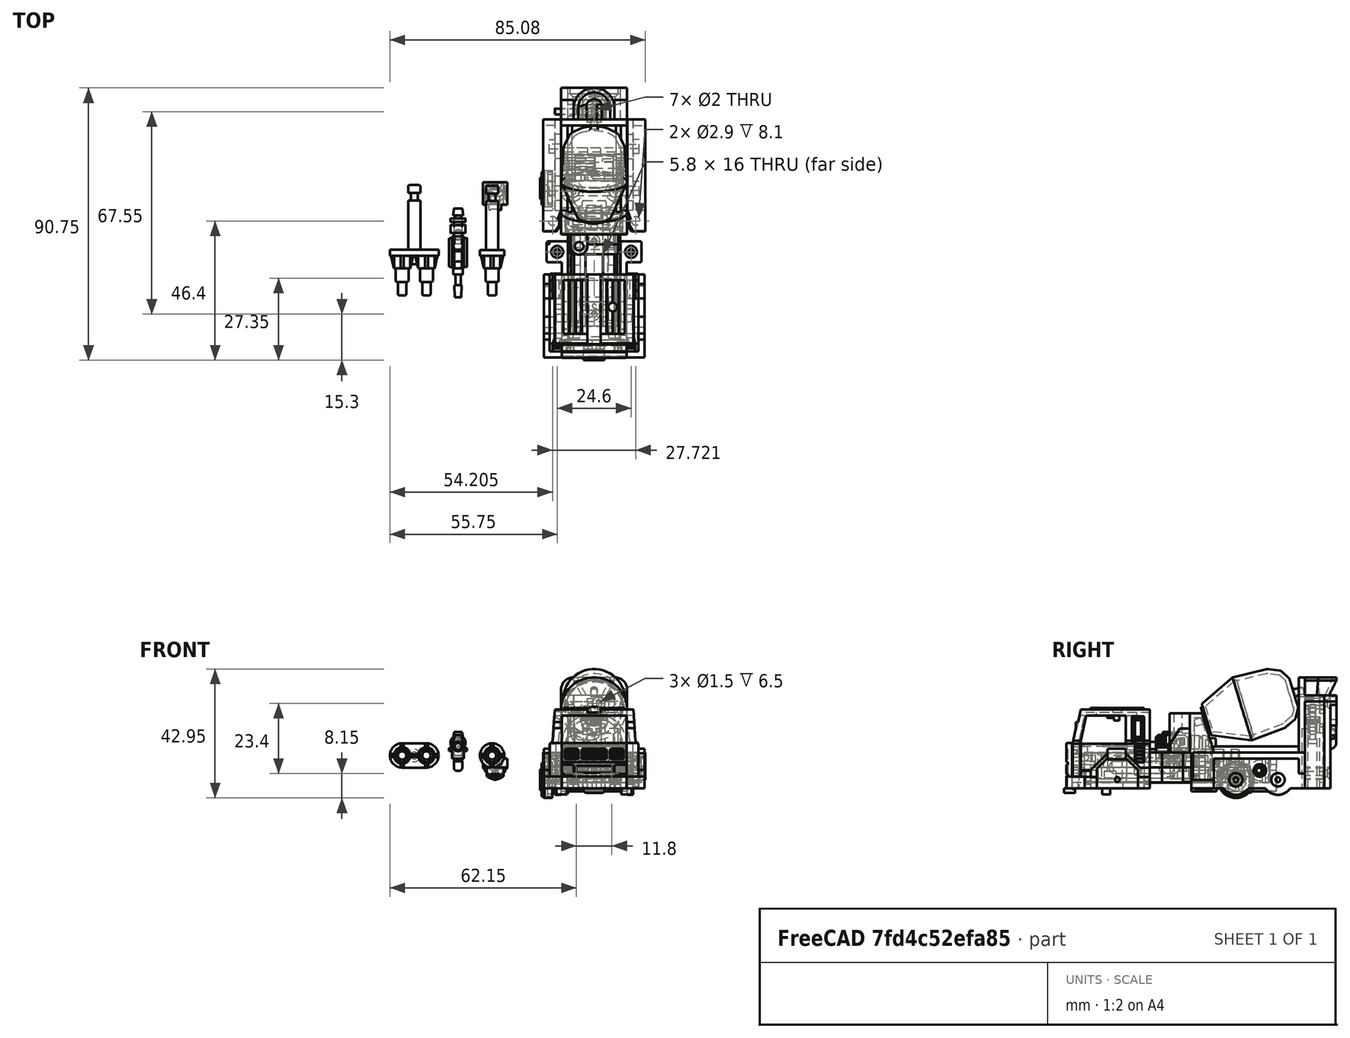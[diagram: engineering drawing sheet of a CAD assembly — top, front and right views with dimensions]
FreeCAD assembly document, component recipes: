
FREECAD ASSEMBLY — COMPONENT RECIPES ("MixMaster")

This assembly document has 25 components, labeled P0..P24 below (a component is one placed body or linked part). 24 of them carry a construction recipe — the FreeCAD feature program that regenerates the part from scratch, quoted from this document or its linked companion documents; the rest are supplied as boundary geometry only. No exploded tour is included for this assembly.
NOTE — document 4 of 4 of this assembly tour. The two overview renders and the header above are repeated from document 1; the component sections below continue where the previous document stopped.
COMPONENT P18 — recipe-attached ("Tire2", modeled in this document).
Construction recipe (the document's own serialized feature program — sketch geometry with constraints, then the solid features built on it; lengths are millimeters unless a unit is written):

FEATURE [Sketcher::SketchObject] Sketch097
  ArcFitTolerance = 1e-06
  AttachmentSupport = -> [XY_Plane008]
  FullyConstrained = true
  MakeInternals = false
  MapMode = 5
  sketch-geometry (1):
    g0: Circle CenterX=0 CenterY=0 CenterZ=0 NormalX=0 NormalY=0 NormalZ=1 AngleXU=0 Radius=6.05
  constraints (2):
    c: Coincident(g0,g-1)
    c: Diameter(g0) = 12.1
FEATURE [PartDesign::Pad] Pad067
  Direction = (0,0,1)
  Length = 3.6
  Length2 = 10
  Profile = -> Sketch097
  ReferenceAxis = -> Sketch097 [N_Axis]
  Refine = true
  Suppressed = false
  Type = 0
FEATURE [Sketcher::SketchObject] Sketch098
  ArcFitTolerance = 1e-06
  AttachmentSupport = -> [Pad067]
  FullyConstrained = true
  MakeInternals = false
  MapMode = 5
  Placement = pos=(0,0,3.6) rot=(0,0,1;0rad)
  sketch-geometry (1):
    g0: Circle CenterX=0 CenterY=0 CenterZ=0 NormalX=0 NormalY=0 NormalZ=1 AngleXU=0 Radius=3.55
  constraints (2):
    c: Coincident(g0,g-1)
    c: Diameter(g0) = 7.1
FEATURE [PartDesign::Pad] Pad068
  BaseFeature = -> Pad067
  Direction = (0,0,1)
  Length = 0.5
  Length2 = 10
  Profile = -> Sketch098
  ReferenceAxis = -> Sketch098 [N_Axis]
  Refine = true
  Suppressed = false
  Type = 0
FEATURE [Sketcher::SketchObject] Sketch099
  ArcFitTolerance = 1e-06
  AttachmentSupport = -> [Pad068]
  ExternalGeometry = -> [Pad068]
  FullyConstrained = true
  MakeInternals = false
  MapMode = 5
  Placement = pos=(0,0,3.6) rot=(0,0,1;0rad)
  sketch-geometry (2):
    g0: Circle CenterX=0 CenterY=0 CenterZ=0 NormalX=0 NormalY=0 NormalZ=1 AngleXU=0 Radius=5
    g1: Circle CenterX=0 CenterY=0 CenterZ=0 NormalX=0 NormalY=0 NormalZ=1 AngleXU=0 Radius=6.05
  constraints (5):
    c: Diameter(g0) = 10
    c: Coincident(g1,g0)
    c: Diameter(g-3) = 12.1
    c: Diameter(g1) = 12.1
    c: Coincident(g0,g-1)
FEATURE [PartDesign::Pocket] Pocket091
  BaseFeature = -> Pad068
  Direction = (0,0,-1)
  Length = 1
  Length2 = 5
  Profile = -> Sketch099
  ReferenceAxis = -> Sketch099 [N_Axis]
  Refine = true
  Suppressed = false
  Type = 0
FEATURE [Sketcher::SketchObject] Sketch100
  ArcFitTolerance = 1e-06
  AttachmentSupport = -> [Pocket091]
  ExternalGeometry = -> [Pocket091]
  FullyConstrained = true
  MakeInternals = false
  MapMode = 5
  Placement = pos=(0,0,3.6) rot=(0,0,1;0rad)
  sketch-geometry (50):
    g0: Circle [constr] CenterX=0 CenterY=0 CenterZ=0 NormalX=0 NormalY=0 NormalZ=1 AngleXU=0 Radius=6.05
    g1: LineSegment StartX=4e-16 StartY=6.05 StartZ=0 EndX=-0.789683 EndY=5.99824 EndZ=0
    g2: LineSegment StartX=-0.789683 StartY=5.99824 StartZ=0 EndX=-1.56586 EndY=5.84385 EndZ=0
    g3: LineSegment StartX=-1.56586 StartY=5.84385 StartZ=0 EndX=-2.31523 EndY=5.58947 EndZ=0
    g4: LineSegment StartX=-2.31523 StartY=5.58947 StartZ=0 EndX=-3.025 EndY=5.23945 EndZ=0
    g5: LineSegment StartX=-3.025 StartY=5.23945 StartZ=0 EndX=-3.68301 EndY=4.79979 EndZ=0
    g6: LineSegment StartX=-3.68301 StartY=4.79979 StartZ=0 EndX=-4.278 EndY=4.278 EndZ=0
    g7: LineSegment StartX=-4.278 StartY=4.278 StartZ=0 EndX=-4.79979 EndY=3.68301 EndZ=0
    g8: LineSegment StartX=-4.79979 StartY=3.68301 StartZ=0 EndX=-5.23945 EndY=3.025 EndZ=0
    g9: LineSegment StartX=-5.23945 StartY=3.025 StartZ=0 EndX=-5.58947 EndY=2.31523 EndZ=0
    g10: LineSegment StartX=-5.58947 StartY=2.31523 StartZ=0 EndX=-5.84385 EndY=1.56586 EndZ=0
    g11: LineSegment StartX=-5.84385 StartY=1.56586 StartZ=0 EndX=-5.99824 EndY=0.789683 EndZ=0
    g12: LineSegment StartX=-5.99824 StartY=0.789683 StartZ=0 EndX=-6.05 EndY=4e-16 EndZ=0
    g13: LineSegment StartX=-6.05 StartY=4e-16 StartZ=0 EndX=-5.99824 EndY=-0.789683 EndZ=0
    g14: LineSegment StartX=-5.99824 StartY=-0.789683 StartZ=0 EndX=-5.84385 EndY=-1.56586 EndZ=0
    g15: LineSegment StartX=-5.84385 StartY=-1.56586 StartZ=0 EndX=-5.58947 EndY=-2.31523 EndZ=0
    g16: LineSegment StartX=-5.58947 StartY=-2.31523 StartZ=0 EndX=-5.23945 EndY=-3.025 EndZ=0
    g17: LineSegment StartX=-5.23945 StartY=-3.025 StartZ=0 EndX=-4.79979 EndY=-3.68301 EndZ=0
    g18: LineSegment StartX=-4.79979 StartY=-3.68301 StartZ=0 EndX=-4.278 EndY=-4.278 EndZ=0
    g19: LineSegment StartX=-4.278 StartY=-4.278 StartZ=0 EndX=-3.68301 EndY=-4.79979 EndZ=0
    g20: LineSegment StartX=-3.68301 StartY=-4.79979 StartZ=0 EndX=-3.025 EndY=-5.23945 EndZ=0
    g21: LineSegment StartX=-3.025 StartY=-5.23945 StartZ=0 EndX=-2.31523 EndY=-5.58947 EndZ=0
    g22: LineSegment StartX=-2.31523 StartY=-5.58947 StartZ=0 EndX=-1.56586 EndY=-5.84385 EndZ=0
    g23: LineSegment StartX=-1.56586 StartY=-5.84385 StartZ=0 EndX=-0.789683 EndY=-5.99824 EndZ=0
    g24: LineSegment StartX=-0.789683 StartY=-5.99824 StartZ=0 EndX=-1e-16 EndY=-6.05 EndZ=0
    g25: LineSegment StartX=-1e-16 StartY=-6.05 StartZ=0 EndX=0.789683 EndY=-5.99824 EndZ=0
    g26: LineSegment StartX=0.789683 StartY=-5.99824 StartZ=0 EndX=1.56586 EndY=-5.84385 EndZ=0
    g27: LineSegment StartX=1.56586 StartY=-5.84385 StartZ=0 EndX=2.31523 EndY=-5.58947 EndZ=0
    g28: LineSegment StartX=2.31523 StartY=-5.58947 StartZ=0 EndX=3.025 EndY=-5.23945 EndZ=0
    g29: LineSegment StartX=3.025 StartY=-5.23945 StartZ=0 EndX=3.68301 EndY=-4.79979 EndZ=0
    g30: LineSegment StartX=3.68301 StartY=-4.79979 StartZ=0 EndX=4.278 EndY=-4.278 EndZ=0
    g31: LineSegment StartX=4.278 StartY=-4.278 StartZ=0 EndX=4.79979 EndY=-3.68301 EndZ=0
    g32: LineSegment StartX=4.79979 StartY=-3.68301 StartZ=0 EndX=5.23945 EndY=-3.025 EndZ=0
    g33: LineSegment StartX=5.23945 StartY=-3.025 StartZ=0 EndX=5.58947 EndY=-2.31523 EndZ=0
    g34: LineSegment StartX=5.58947 StartY=-2.31523 StartZ=0 EndX=5.84385 EndY=-1.56586 EndZ=0
    g35: LineSegment StartX=5.84385 StartY=-1.56586 StartZ=0 EndX=5.99824 EndY=-0.789683 EndZ=0
    g36: LineSegment StartX=5.99824 StartY=-0.789683 StartZ=0 EndX=6.05 EndY=0 EndZ=0
    g37: LineSegment StartX=6.05 StartY=0 StartZ=0 EndX=5.99824 EndY=0.789683 EndZ=0
    g38: LineSegment StartX=5.99824 StartY=0.789683 StartZ=0 EndX=5.84385 EndY=1.56586 EndZ=0
    g39: LineSegment StartX=5.84385 StartY=1.56586 StartZ=0 EndX=5.58947 EndY=2.31523 EndZ=0
    g40: LineSegment StartX=5.58947 StartY=2.31523 StartZ=0 EndX=5.23945 EndY=3.025 EndZ=0
    g41: LineSegment StartX=5.23945 StartY=3.025 StartZ=0 EndX=4.79979 EndY=3.68301 EndZ=0
    g42: LineSegment StartX=4.79979 StartY=3.68301 StartZ=0 EndX=4.278 EndY=4.278 EndZ=0
    g43: LineSegment StartX=4.278 StartY=4.278 StartZ=0 EndX=3.68301 EndY=4.79979 EndZ=0
    g44: LineSegment StartX=3.68301 StartY=4.79979 StartZ=0 EndX=3.025 EndY=5.23945 EndZ=0
    g45: LineSegment StartX=3.025 StartY=5.23945 StartZ=0 EndX=2.31523 EndY=5.58947 EndZ=0
    g46: LineSegment StartX=2.31523 StartY=5.58947 StartZ=0 EndX=1.56586 EndY=5.84385 EndZ=0
    g47: LineSegment StartX=1.56586 StartY=5.84385 StartZ=0 EndX=0.789683 EndY=5.99824 EndZ=0
    g48: LineSegment StartX=0.789683 StartY=5.99824 StartZ=0 EndX=4e-16 EndY=6.05 EndZ=0
    g49: Circle [constr] CenterX=0 CenterY=0 CenterZ=0 NormalX=0 NormalY=0 NormalZ=1 AngleXU=0 Radius=6.05
  constraints (102):
    c: Coincident(g0,g-1)
    c: Coincident(g1,g2)
    c: Coincident(g2,g3)
    c: Coincident(g3,g4)
    c: Coincident(g4,g5)
    c: Coincident(g5,g6)
    c: Coincident(g6,g7)
    c: Coincident(g7,g8)
    c: Coincident(g8,g9)
    c: Coincident(g9,g10)
    c: Coincident(g10,g11)
    c: Coincident(g11,g12)
    c: Coincident(g12,g13)
    c: Coincident(g13,g14)
    c: Coincident(g14,g15)
    c: Coincident(g15,g16)
    c: Coincident(g16,g17)
    c: Coincident(g17,g18)
    c: Coincident(g18,g19)
    c: Coincident(g19,g20)
    c: Coincident(g20,g21)
    c: Coincident(g21,g22)
    c: Coincident(g22,g23)
    c: Coincident(g23,g24)
    c: Coincident(g24,g25)
    c: Coincident(g25,g26)
    c: Coincident(g26,g27)
    c: Coincident(g27,g28)
    c: Coincident(g28,g29)
    c: Coincident(g29,g30)
    c: Coincident(g30,g31)
    c: Coincident(g31,g32)
    c: Coincident(g32,g33)
    c: Coincident(g33,g34)
    c: Coincident(g34,g35)
    c: Coincident(g35,g36)
    c: Coincident(g36,g37)
    c: Coincident(g37,g38)
    c: Coincident(g38,g39)
    c: Coincident(g39,g40)
    c: Coincident(g40,g41)
    c: Coincident(g41,g42)
    c: Coincident(g42,g43)
    c: Coincident(g43,g44)
    c: Coincident(g44,g45)
    c: Coincident(g45,g46)
    c: Coincident(g46,g47)
    c: Coincident(g47,g48)
    c: Coincident(g48,g1)
    c: Equal(g1, g2-g48) x47
    c: PointOnObject(g1,g49)
    c: PointOnObject(g2,g49)
    c: PointOnObject(g3,g49)
    c: PointOnObject(g4,g49)
    c: PointOnObject(g5,g49)
    c: PointOnObject(g6,g49)
    c: PointOnObject(g7,g49)
    c: PointOnObject(g8,g49)
    c: PointOnObject(g9,g49)
    c: PointOnObject(g10,g49)
    c: PointOnObject(g11,g49)
    c: PointOnObject(g12,g49)
    c: PointOnObject(g13,g49)
    c: PointOnObject(g14,g49)
    c: PointOnObject(g15,g49)
    c: PointOnObject(g16,g49)
    c: PointOnObject(g17,g49)
    c: PointOnObject(g18,g49)
    c: PointOnObject(g19,g49)
    c: PointOnObject(g20,g49)
    c: PointOnObject(g21,g49)
    c: PointOnObject(g22,g49)
    c: PointOnObject(g23,g49)
    c: PointOnObject(g24,g49)
    c: PointOnObject(g25,g49)
    c: PointOnObject(g26,g49)
    c: PointOnObject(g27,g49)
    c: PointOnObject(g28,g49)
    c: PointOnObject(g29,g49)
    c: PointOnObject(g30,g49)
    c: PointOnObject(g31,g49)
    c: PointOnObject(g32,g49)
    c: PointOnObject(g33,g49)
    c: PointOnObject(g34,g49)
    c: PointOnObject(g35,g49)
    c: PointOnObject(g36,g49)
    c: PointOnObject(g37,g49)
    c: PointOnObject(g38,g49)
    c: PointOnObject(g39,g49)
    c: PointOnObject(g40,g49)
    c: PointOnObject(g41,g49)
    c: PointOnObject(g42,g49)
    c: PointOnObject(g43,g49)
    c: PointOnObject(g44,g49)
    c: PointOnObject(g45,g49)
    c: PointOnObject(g46,g49)
    c: PointOnObject(g47,g49)
    c: PointOnObject(g48,g49)
    c: Coincident(g49,g0)
    c: PointOnObject(g48,g0)
    c: PointOnObject(g1,g-3)
    c: DistanceY(g0,g36) = 0
FEATURE [PartDesign::Pad] Pad069
  BaseFeature = -> Pocket091
  Direction = (0,0,1)
  Length = 1
  Length2 = 10
  Profile = -> Sketch100
  ReferenceAxis = -> Sketch100 [N_Axis]
  Refine = true
  Reversed = true
  Suppressed = false
  Type = 0
FEATURE [PartDesign::Chamfer] Chamfer
  Angle = 45
  Base = -> Pad069 [Edge137,Edge139,Edge141,Edge143,Edge145,Edge147,Edge149,Edge151,Edge153,Edge135,Edge133,Edge131,Edge129,Edge127,Edge125,Edge123,Edge121,Edge119,Edge117,Edge115,Edge113,Edge111,Edge109,Edge107,Edge105,Edge103,Edge101,Edge194,Edge193,Edge191,Edge189,Edge187,Edge185,Edge183,Edge181,Edge179,Edge177,Edge175,Edge173,Edge171,+8 more]
  BaseFeature = -> Pad069
  ChamferType = 0
  FlipDirection = false
  Refine = true
  Size = 0.99
  Size2 = 1
  SupportTransform = false
  Suppressed = false
  UseAllEdges = false
FEATURE [PartDesign::Pad] Pad070
  BaseFeature = -> Chamfer
  Direction = (-0.312745,0.634185,0.707107)
  Length = 0.2
  Length2 = 10
  Profile = -> Chamfer [Face44]
  Refine = true
  Suppressed = false
  Type = 0
FEATURE [PartDesign::Pad] Pad071
  BaseFeature = -> Pad070
  Direction = (0.587938,-0.392847,0.707107)
  Length = 0.2
  Length2 = 10
  Profile = -> Pad070 [Face45]
  Refine = true
  Suppressed = false
  Type = 0
FEATURE [PartDesign::Pad] Pad072
  BaseFeature = -> Pad071
  Direction = (-0.13795,0.69352,0.707107)
  Length = 0.2
  Length2 = 10
  Profile = -> Pad071 [Face48]
  Refine = true
  Suppressed = false
  Type = 0
FEATURE [PartDesign::Pad] Pad073
  BaseFeature = -> Pad072
  Direction = (0.046247,0.705593,0.707107)
  Length = 0.2
  Length2 = 10
  Profile = -> Pad072 [Face50]
  Refine = true
  Suppressed = false
  Type = 0
FEATURE [PartDesign::Pad] Pad074
  BaseFeature = -> Pad073
  Direction = (0.227292,0.669581,0.707107)
  Length = 0.2
  Length2 = 10
  Profile = -> Pad073 [Face52]
  Refine = true
  Suppressed = false
  Type = 0
FEATURE [PartDesign::Pad] Pad075
  BaseFeature = -> Pad074
  Direction = (0.392847,0.587938,0.707107)
  Length = 0.2
  Length2 = 10
  Profile = -> Pad074 [Face56]
  Refine = true
  Suppressed = false
  Type = 0
FEATURE [PartDesign::Pad] Pad076
  BaseFeature = -> Pad075
  Direction = (0.531631,0.466228,0.707107)
  Length = 0.2
  Length2 = 10
  Profile = -> Pad075 [Face60]
  Refine = true
  Suppressed = false
  Type = 0
FEATURE [PartDesign::Pad] Pad077
  BaseFeature = -> Pad076
  Direction = (0.634185,0.312745,0.707107)
  Length = 0.2
  Length2 = 10
  Profile = -> Pad076 [Face57]
  Refine = true
  Suppressed = false
  Type = 0
FEATURE [PartDesign::Pad] Pad078
  BaseFeature = -> Pad077
  Direction = (-0.466228,0.531631,0.707107)
  Length = 0.2
  Length2 = 10
  Profile = -> Pad077 [Face40]
  Refine = true
  Suppressed = false
  Type = 0
FEATURE [PartDesign::Pad] Pad079
  BaseFeature = -> Pad078
  Direction = (-0.587938,0.392847,0.707107)
  Length = 0.2
  Length2 = 10
  Profile = -> Pad078 [Face36]
  Refine = true
  Suppressed = false
  Type = 0
FEATURE [PartDesign::Pad] Pad080
  BaseFeature = -> Pad079
  Direction = (-0.669581,0.227292,0.707107)
  Length = 0.2
  Length2 = 10
  Profile = -> Pad079 [Face32]
  Refine = true
  Suppressed = false
  Type = 0
FEATURE [PartDesign::Pad] Pad081
  BaseFeature = -> Pad080
  Direction = (-0.705593,0.046247,0.707107)
  Length = 0.2
  Length2 = 10
  Profile = -> Pad080 [Face28]
  Refine = true
  Suppressed = false
  Type = 0
FEATURE [PartDesign::Pad] Pad082
  BaseFeature = -> Pad081
  Direction = (-0.69352,-0.13795,0.707107)
  Length = 0.2
  Length2 = 10
  Profile = -> Pad081 [Face24]
  Refine = true
  Suppressed = false
  Type = 0
FEATURE [PartDesign::Pad] Pad083
  BaseFeature = -> Pad082
  Direction = (-0.634185,-0.312745,0.707107)
  Length = 0.2
  Length2 = 10
  Profile = -> Pad082 [Face20]
  Refine = true
  Suppressed = false
  Type = 0
FEATURE [PartDesign::Pad] Pad084
  BaseFeature = -> Pad083
  Direction = (0.69352,0.13795,0.707107)
  Length = 0.2
  Length2 = 10
  Profile = -> Pad083 [Face53]
  Refine = true
  Suppressed = false
  Type = 0
FEATURE [PartDesign::Pad] Pad085
  BaseFeature = -> Pad084
  Direction = (0.705593,-0.046247,0.707107)
  Length = 0.2
  Length2 = 10
  Profile = -> Pad084 [Face3]
  Refine = true
  Suppressed = false
  Type = 0
FEATURE [PartDesign::Pad] Pad086
  BaseFeature = -> Pad085
  Direction = (0.669581,-0.227292,0.707107)
  Length = 0.2
  Length2 = 10
  Profile = -> Pad085 [Face17]
  Refine = true
  Suppressed = false
  Type = 0
FEATURE [PartDesign::Pad] Pad087
  BaseFeature = -> Pad086
  Direction = (0.466228,-0.531631,0.707107)
  Length = 0.2
  Length2 = 10
  Profile = -> Pad086 [Face99]
  Refine = true
  Suppressed = false
  Type = 0
FEATURE [PartDesign::Pad] Pad088
  BaseFeature = -> Pad087
  Direction = (-0.531631,-0.466228,0.707107)
  Length = 0.2
  Length2 = 10
  Profile = -> Pad087 [Face75]
  Refine = true
  Suppressed = false
  Type = 0
FEATURE [PartDesign::Pad] Pad089
  BaseFeature = -> Pad088
  Direction = (-0.392847,-0.587938,0.707107)
  Length = 0.2
  Length2 = 10
  Profile = -> Pad088 [Face79]
  Refine = true
  Suppressed = false
  Type = 0
FEATURE [PartDesign::Pad] Pad090
  BaseFeature = -> Pad089
  Direction = (-0.227292,-0.669581,0.707107)
  Length = 0.2
  Length2 = 10
  Profile = -> Pad089 [Face83]
  Refine = true
  Suppressed = false
  Type = 0
FEATURE [PartDesign::Pad] Pad091
  BaseFeature = -> Pad090
  Direction = (-0.046247,-0.705593,0.707107)
  Length = 0.2
  Length2 = 10
  Profile = -> Pad090 [Face87]
  Refine = true
  Suppressed = false
  Type = 0
FEATURE [PartDesign::Pad] Pad092
  BaseFeature = -> Pad091
  Direction = (0.312745,-0.634185,0.707107)
  Length = 0.2
  Length2 = 10
  Profile = -> Pad091 [Face95]
  Refine = true
  Suppressed = false
  Type = 0
FEATURE [PartDesign::Pad] Pad093
  BaseFeature = -> Pad092
  Direction = (0.13795,-0.69352,0.707107)
  Length = 0.2
  Length2 = 10
  Profile = -> Pad092 [Face91]
  Refine = true
  Suppressed = false
  Type = 0
FEATURE [Sketcher::SketchObject] Sketch101
  ArcFitTolerance = 1e-06
  AttachmentSupport = -> [Pad093]
  FullyConstrained = true
  MakeInternals = false
  MapMode = 5
  Placement = pos=(0,0,3.6) rot=(0,0,1;0rad)
  sketch-geometry (2):
    g0: Circle CenterX=0 CenterY=0 CenterZ=0 NormalX=0 NormalY=0 NormalZ=1 AngleXU=0 Radius=5.5
    g1: Circle CenterX=0 CenterY=0 CenterZ=0 NormalX=0 NormalY=0 NormalZ=1 AngleXU=0 Radius=4.5
  constraints (4):
    c: Coincident(g0,g-1)
    c: Diameter(g0) = 11
    c: Coincident(g1,g0)
    c: Diameter(g1) = 9
FEATURE [PartDesign::Pocket] Pocket092
  BaseFeature = -> Pad093
  Direction = (0,0,-1)
  Length = 5
  Length2 = 5
  Profile = -> Sketch101 [Edge2,Edge1]
  ReferenceAxis = -> Sketch101 [N_Axis]
  Refine = true
  Reversed = true
  Suppressed = false
  Type = 0
FEATURE [Sketcher::SketchObject] Sketch102
  ArcFitTolerance = 1e-06
  AttachmentSupport = -> [Pocket092]
  ExternalGeometry = -> [Pocket092]
  FullyConstrained = false
  MakeInternals = false
  MapMode = 5
  Placement = pos=(0,0,0) rot=(1,0,0;3.14159rad)
  sketch-geometry (2):
    g0: Circle CenterX=0 CenterY=0 CenterZ=0 NormalX=0 NormalY=0 NormalZ=1 AngleXU=0 Radius=6.05
    g1: Circle CenterX=0 CenterY=0 CenterZ=0 NormalX=0 NormalY=0 NormalZ=1 AngleXU=0 Radius=6.5
  constraints (3):
    c: Coincident(g0,g-1)
    c: Coincident(g1,g0)
    c: Diameter(g1) = 13
FEATURE [PartDesign::Pocket] Pocket093
  BaseFeature = -> Pocket092
  Direction = (0,0,1)
  Length = 5
  Length2 = 5
  Profile = -> Sketch102
  ReferenceAxis = -> Sketch102 [N_Axis]
  Refine = true
  Suppressed = false
  Type = 0
FEATURE [Sketcher::SketchObject] Sketch103
  ArcFitTolerance = 1e-06
  AttachmentSupport = -> [Pocket093]
  FullyConstrained = true
  MakeInternals = false
  MapMode = 5
  Placement = pos=(0,0,4.1) rot=(0,0,1;0rad)
  sketch-geometry (1):
    g0: Circle CenterX=0 CenterY=0 CenterZ=0 NormalX=0 NormalY=0 NormalZ=1 AngleXU=0 Radius=1.05
  constraints (2):
    c: Coincident(g0,g-1)
    c: Diameter(g0) = 2.1
FEATURE [PartDesign::Pocket] Pocket094
  BaseFeature = -> Pocket093
  Direction = (0,0,-1)
  Length = 5
  Length2 = 5
  Profile = -> Sketch103
  ReferenceAxis = -> Sketch103 [N_Axis]
  Refine = true
  Suppressed = false
  Type = 0
FEATURE [Sketcher::SketchObject] Sketch104
  ArcFitTolerance = 1e-06
  AttachmentSupport = -> [Pocket094]
  FullyConstrained = true
  MakeInternals = false
  MapMode = 5
  Placement = pos=(0,0,4.1) rot=(0,0,1;0rad)
  sketch-geometry (1):
    g0: Circle CenterX=0 CenterY=0 CenterZ=0 NormalX=0 NormalY=0 NormalZ=1 AngleXU=0 Radius=1.75
  constraints (2):
    c: Coincident(g0,g-1)
    c: Diameter(g0) = 3.5
FEATURE [PartDesign::Pocket] Pocket095
  BaseFeature = -> Pocket094
  Direction = (0,0,-1)
  Length = 1
  Length2 = 5
  Profile = -> Sketch104
  ReferenceAxis = -> Sketch104 [N_Axis]
  Refine = true
  Suppressed = false
  Type = 0
FEATURE [Sketcher::SketchObject] Sketch105
  ArcFitTolerance = 1e-06
  AttachmentSupport = -> [Pocket095]
  ExternalGeometry = -> [Pocket095]
  FullyConstrained = true
  MakeInternals = false
  MapMode = 5
  Placement = pos=(0,0,4.1) rot=(0,0,1;0rad)
  sketch-geometry (12):
    g0: Circle CenterX=0 CenterY=2.65 CenterZ=0 NormalX=0 NormalY=0 NormalZ=1 AngleXU=0 Radius=0.25
    g1: Circle CenterX=2.65 CenterY=0 CenterZ=0 NormalX=0 NormalY=0 NormalZ=1 AngleXU=0 Radius=0.25
    g2: Circle CenterX=0 CenterY=-2.65 CenterZ=0 NormalX=0 NormalY=0 NormalZ=1 AngleXU=0 Radius=0.25
    g3: Circle CenterX=-2.65 CenterY=0 CenterZ=0 NormalX=0 NormalY=0 NormalZ=1 AngleXU=0 Radius=0.25
    g4: Circle CenterX=1.87383 CenterY=1.87383 CenterZ=0 NormalX=0 NormalY=0 NormalZ=1 AngleXU=0 Radius=0.25
    g5: Circle CenterX=1.87383 CenterY=-1.87383 CenterZ=0 NormalX=0 NormalY=0 NormalZ=1 AngleXU=0 Radius=0.25
    g6: Circle CenterX=-1.87383 CenterY=-1.87383 CenterZ=0 NormalX=0 NormalY=0 NormalZ=1 AngleXU=0 Radius=0.25
    g7: Circle CenterX=-1.87383 CenterY=1.87383 CenterZ=0 NormalX=0 NormalY=0 NormalZ=1 AngleXU=0 Radius=0.25
    g8: LineSegment StartX=1.87383 StartY=1.87383 StartZ=0 EndX=0 EndY=0 EndZ=0
    g9: LineSegment StartX=0 StartY=0 StartZ=0 EndX=1.87383 EndY=-1.87383 EndZ=0
    g10: LineSegment StartX=0 StartY=0 StartZ=0 EndX=-1.87383 EndY=-1.87383 EndZ=0
    g11: LineSegment StartX=0 StartY=0 StartZ=0 EndX=-1.87383 EndY=1.87383 EndZ=0
  constraints (34):
    c: PointOnObject(g0,g-2)
    c: Diameter(g-3) = 7.1
    c: Diameter(g-4) = 3.5
    c: DistanceY(g-1,g0) = 2.65
    c: Diameter(g0) = 0.5
    c: PointOnObject(g1,g-1)
    c: PointOnObject(g2,g-2)
    c: PointOnObject(g3,g-1)
    c: Diameter(g3) = 0.5
    c: Diameter(g1) = 0.5
    c: Diameter(g2) = 0.5
    c: DistanceX(g3,g-1) = 2.65
    c: DistanceX(g-1,g1) = 2.65
    c: DistanceY(g2,g-1) = 2.65
    c: Diameter(g7) = 0.5
    c: Diameter(g4) = 0.5
    c: Diameter(g5) = 0.5
    c: Diameter(g6) = 0.5
    c: Distance(g-1,g6) = 2.65
    c: Distance(g-1,g5) = 2.65
    c: Distance(g-1,g4) = 2.65
    c: Distance(g-1,g7) = 2.65
    c: Coincident(g8,g4)
    c: Coincident(g8,g-1)
    c: Angle(g-1,g8) = 0.785398
    c: Coincident(g9,g8)
    c: Coincident(g9,g5)
    c: Coincident(g10,g8)
    c: Coincident(g10,g6)
    c: Coincident(g11,g8)
    c: Coincident(g11,g7)
    c: Angle(g9,g-1) = 0.785398
    c: Angle(g-2,g10) = 2.35619
    c: Angle(g-1,g11) = 2.35619
FEATURE [PartDesign::Pocket] Pocket096
  BaseFeature = -> Pocket095
  Direction = (0,0,-1)
  Length = 0.2
  Length2 = 5
  Profile = -> Sketch105 [Edge8,Edge4,Edge7,Edge3,Edge6,Edge2,Edge5,Edge1]
  ReferenceAxis = -> Sketch105 [N_Axis]
  Refine = true
  Suppressed = false
  Type = 0
FEATURE [Sketcher::SketchObject] Sketch106
  ArcFitTolerance = 1e-06
  AttachmentSupport = -> [Pocket096]
  FullyConstrained = true
  MakeInternals = false
  MapMode = 5
  Placement = pos=(0,0,0) rot=(1,0,0;3.14159rad)
  sketch-geometry (1):
    g0: Circle CenterX=0 CenterY=0 CenterZ=0 NormalX=0 NormalY=0 NormalZ=1 AngleXU=0 Radius=2.5
  constraints (2):
    c: Coincident(g0,g-1)
    c: Diameter(g0) = 5
FEATURE [PartDesign::Pocket] Pocket097
  BaseFeature = -> Pocket096
  Direction = (0,0,1)
  Length = 1.5
  Length2 = 5
  Profile = -> Sketch106
  ReferenceAxis = -> Sketch106 [N_Axis]
  Refine = true
  Suppressed = false
  Type = 0
FEATURE [Sketcher::SketchObject] Sketch107
  ArcFitTolerance = 1e-06
  AttachmentSupport = -> [Pocket097]
  FullyConstrained = true
  MakeInternals = false
  MapMode = 5
  Placement = pos=(0,0,0) rot=(1,0,0;3.14159rad)
  sketch-geometry (2):
    g0: Circle CenterX=0 CenterY=0 CenterZ=0 NormalX=0 NormalY=0 NormalZ=1 AngleXU=0 Radius=4.75
    g1: Circle CenterX=0 CenterY=0 CenterZ=0 NormalX=0 NormalY=0 NormalZ=1 AngleXU=0 Radius=5.5
  constraints (4):
    c: Coincident(g0,g-1)
    c: Coincident(g1,g0)
    c: Diameter(g0) = 9.5
    c: Diameter(g1) = 11
FEATURE [PartDesign::Pocket] Pocket098
  BaseFeature = -> Pocket097
  Direction = (0,0,1)
  Length = 1.5
  Length2 = 5
  Profile = -> Sketch107
  ReferenceAxis = -> Sketch107 [N_Axis]
  Refine = true
  Suppressed = false
  Type = 0
FEATURE [PartDesign::Body] Body007  label="Tire1"
  AllowCompound = false
  Group = -> [Sketch097,Pad067,Sketch098,Pad068,Sketch099,Pocket091,Sketch100,Pad069,Chamfer,Pad070,Pad071,Pad072,Pad073,Pad074,Pad075,Pad076,Pad077,Pad078,Pad079,Pad080,Pad081,Pad082,Pad083,Pad084,Pad085,Pad086,Pad087,Pad088,Pad089,Pad090,Pad091,Pad092,Pad093,Sketch101,Pocket092,Sketch102,Pocket093,Sketch103,Pocket094,Sketch104,Pocket095,Sketch105,Pocket096,Sketch106,Pocket097,Sketch107,Pocket098]
  Origin = -> Origin008
  Placement = pos=(30.1,12.5,-8.1) rot=(0.707107,0,-0.707107;3.14159rad)
  Tip = -> Pocket098
COMPONENT P19 — recipe-attached ("Pre_Left_Arm", modeled in this document).
Construction recipe (the document's own serialized feature program — sketch geometry with constraints, then the solid features built on it; lengths are millimeters unless a unit is written):

FEATURE [PartDesign::SubShapeBinder] Binder002
  BindCopyOnChange = 0
  BindMode = 2
  ClaimChildren = false
  Fuse = false
  MakeFace = true
  OffsetFill = false
  OffsetIntersection = false
  OffsetJoinType = 0
  OffsetOpenResult = false
  PartialLoad = false
  Refine = true
  Relative = true
  _Version = 2
FEATURE [Sketcher::SketchObject] Sketch071
  ArcFitTolerance = 1e-06
  AttachmentSupport = -> [Binder002]
  FullyConstrained = true
  MakeInternals = false
  MapMode = 5
  Placement = pos=(5.47474,0,5.62e-14) rot=(0.57735,0.57735,0.57735;2.0944rad)
  sketch-geometry (4):
    g0: LineSegment StartX=-2 StartY=-1 StartZ=0 EndX=-2 EndY=-9 EndZ=0
    g1: LineSegment StartX=-2 StartY=-9 StartZ=0 EndX=5 EndY=-9 EndZ=0
    g2: LineSegment StartX=5 StartY=-9 StartZ=0 EndX=5 EndY=-1 EndZ=0
    g3: LineSegment StartX=5 StartY=-1 StartZ=0 EndX=-2 EndY=-1 EndZ=0
  constraints (13):
    c: Vertical(g0)
    c: Vertical(g2)
    c: Horizontal(g1)
    c: Horizontal(g3)
    c: DistanceX(g0,g-1) = 2
    c: DistanceX(g-1,g2) = 5
    c: Coincident(g2,g3)
    c: DistanceY(g3,g-1) = 1
    c: DistanceY(g0,g0) = 8
    c: Coincident(g0,g3)
    c: DistanceX(g1,g1) = 7
    c: DistanceY(g2,g2) = 8
    c: Coincident(g1,g2)
FEATURE [PartDesign::Pad] Pad058
  Direction = (1,0,1.02e-14)
  Length = 2
  Length2 = 10
  Profile = -> Sketch071
  ReferenceAxis = -> Sketch071 [N_Axis]
  Refine = true
  Suppressed = false
  Type = 0
FEATURE [Sketcher::SketchObject] Sketch072
  ArcFitTolerance = 1e-06
  AttachmentSupport = -> [Pad058]
  FullyConstrained = true
  MakeInternals = false
  MapMode = 5
  Placement = pos=(7.47474,0,7.63e-14) rot=(0.57735,0.57735,0.57735;2.0944rad)
  sketch-geometry (1):
    g0: Circle CenterX=1.5 CenterY=-5 CenterZ=0 NormalX=0 NormalY=0 NormalZ=1 AngleXU=0 Radius=3.4
  constraints (3):
    c: Diameter(g0) = 6.8
    c: DistanceY(g0,g-1) = 5
    c: DistanceX(g-1,g0) = 1.5
FEATURE [PartDesign::Pad] Pad059
  BaseFeature = -> Pad058
  Direction = (1,0,1.02e-14)
  Length = 2.7
  Length2 = 10
  Profile = -> Sketch072
  ReferenceAxis = -> Sketch072 [N_Axis]
  Refine = true
  Suppressed = false
  Type = 0
FEATURE [Sketcher::SketchObject] Sketch073
  ArcFitTolerance = 1e-06
  AttachmentSupport = -> [Pad059]
  FullyConstrained = true
  MakeInternals = false
  MapMode = 5
  Placement = pos=(10.1747,0,1.028e-13) rot=(0.57735,0.57735,0.57735;2.0944rad)
  sketch-geometry (1):
    g0: Circle CenterX=1.5 CenterY=-5 CenterZ=0 NormalX=0 NormalY=0 NormalZ=1 AngleXU=0 Radius=1.4
  constraints (3):
    c: Diameter(g0) = 2.8
    c: DistanceX(g-1,g0) = 1.5
    c: DistanceY(g0,g-1) = 5
FEATURE [PartDesign::Pocket] Pocket183
  BaseFeature = -> Pad059
  Direction = (-1,0,-1.02e-14)
  Length = 5
  Length2 = 5
  Profile = -> Sketch073
  ReferenceAxis = -> Sketch073 [N_Axis]
  Refine = true
  Suppressed = false
  Type = 0
FEATURE [PartDesign::Pad] Pad060
  BaseFeature = -> Pocket183
  Direction = (-1,0,-1.02e-14)
  Length = 2
  Length2 = 10
  Profile = -> Pocket183 [Face4]
  Refine = true
  Suppressed = false
  Type = 0
FEATURE [Sketcher::SketchObject] Sketch074
  ArcFitTolerance = 1e-06
  AttachmentSupport = -> [Pad060]
  ExternalGeometry = -> [Pad060]
  FullyConstrained = true
  MakeInternals = false
  MapMode = 5
  Placement = pos=(3.47474,0,3.55e-14) rot=(0.57735,-0.57735,-0.57735;2.0944rad)
  sketch-geometry (1):
    g0: Circle CenterX=-1.5 CenterY=-5 CenterZ=0 NormalX=0 NormalY=0 NormalZ=1 AngleXU=0 Radius=2.1
  constraints (2):
    c: Diameter(g0) = 4.2
    c: Coincident(g0,g-3)
FEATURE [PartDesign::Pocket] Pocket184
  BaseFeature = -> Pad060
  Direction = (1,0,1.02e-14)
  Length = 4.7
  Length2 = 5
  Profile = -> Sketch074
  ReferenceAxis = -> Sketch074 [N_Axis]
  Refine = true
  Suppressed = false
  Type = 0
FEATURE [Sketcher::SketchObject] Sketch075
  ArcFitTolerance = 1e-06
  AttachmentSupport = -> [Pocket184]
  ExternalGeometry = -> [Pocket184]
  FullyConstrained = true
  MakeInternals = false
  MapMode = 5
  Placement = pos=(3.47474,0,3.55e-14) rot=(0.57735,-0.57735,-0.57735;2.0944rad)
  sketch-geometry (8):
    g0: LineSegment StartX=-16.5 StartY=1 StartZ=0 EndX=-16.5 EndY=-11 EndZ=0
    g1: LineSegment StartX=-16.5 StartY=-11 StartZ=0 EndX=13.8 EndY=-11 EndZ=0
    g2: LineSegment StartX=13.8 StartY=-11 StartZ=0 EndX=13.8 EndY=1 EndZ=0
    g3: LineSegment StartX=13.8 StartY=1 StartZ=0 EndX=-16.5 EndY=1 EndZ=0
    g4: LineSegment StartX=-5 StartY=-1 StartZ=0 EndX=-5 EndY=-9 EndZ=0
    g5: LineSegment StartX=-5 StartY=-9 StartZ=0 EndX=2 EndY=-9 EndZ=0
    g6: LineSegment StartX=2 StartY=-9 StartZ=0 EndX=2 EndY=-1 EndZ=0
    g7: LineSegment StartX=2 StartY=-1 StartZ=0 EndX=-5 EndY=-1 EndZ=0
  constraints (21):
    c: Coincident(g0,g1)
    c: Coincident(g1,g2)
    c: Coincident(g2,g3)
    c: Coincident(g3,g0)
    c: Vertical(g0)
    c: Vertical(g2)
    c: Horizontal(g1)
    c: Horizontal(g3)
    c: Coincident(g4,g5)
    c: Coincident(g5,g6)
    c: Coincident(g6,g7)
    c: Coincident(g7,g4)
    c: Vertical(g6)
    c: Horizontal(g7)
    c: DistanceY(g0,g0) = 12
    c: Coincident(g4,g-5)
    c: Coincident(g4,g-5)
    c: Coincident(g5,g-4)
    c: DistanceX(g0,g4) = 11.5
    c: DistanceX(g6,g2) = 11.8
    c: DistanceY(g1,g5) = 2
FEATURE [PartDesign::Pad] Pad061
  BaseFeature = -> Pocket184
  Direction = (-1,0,-1.02e-14)
  Length = 2
  Length2 = 10
  Profile = -> Sketch075
  ReferenceAxis = -> Sketch075 [N_Axis]
  Refine = true
  Reversed = true
  Suppressed = false
  Type = 0
FEATURE [Sketcher::SketchObject] Sketch076
  ArcFitTolerance = 1e-06
  AttachmentSupport = -> [Pad061]
  ExternalGeometry = -> [Pad061]
  FullyConstrained = true
  MakeInternals = false
  MapMode = 5
  Placement = pos=(3.47474,0,3.55e-14) rot=(0.57735,-0.57735,-0.57735;2.0944rad)
  sketch-geometry (6):
    g0: LineSegment StartX=-16.5 StartY=1 StartZ=0 EndX=13.8 EndY=1 EndZ=0
    g1: LineSegment StartX=13.8 StartY=1 StartZ=0 EndX=13.8 EndY=-1 EndZ=0
    g2: LineSegment StartX=13.8 StartY=-1 StartZ=0 EndX=-14.5 EndY=-1 EndZ=0
    g3: LineSegment StartX=-14.5 StartY=-1 StartZ=0 EndX=-14.5 EndY=-6 EndZ=0
    g4: LineSegment StartX=-14.5 StartY=-6 StartZ=0 EndX=-16.5 EndY=-6 EndZ=0
    g5: LineSegment StartX=-16.5 StartY=-6 StartZ=0 EndX=-16.5 EndY=1 EndZ=0
  constraints (17):
    c: Coincident(g1,g0)
    c: Coincident(g2,g1)
    c: Horizontal(g2)
    c: Coincident(g3,g2)
    c: Vertical(g3)
    c: Coincident(g4,g3)
    c: Horizontal(g4)
    c: Coincident(g5,g4)
    c: Coincident(g5,g0)
    c: DistanceY(g2,g0) = 2
    c: DistanceY(g5,g5) = 7
    c: DistanceX(g2,g-3) = 13
    c: DistanceY(g-3,g2) = 4
    c: DistanceX(g4,g4) = 2
    c: Vertical(g1)
    c: DistanceX(g0,g-1) = 16.5
    c: Coincident(g0,g-4)
FEATURE [PartDesign::Pad] Pad062
  BaseFeature = -> Pad061
  Direction = (-1,0,-1.02e-14)
  Length = 4
  Length2 = 10
  Profile = -> Sketch076
  ReferenceAxis = -> Sketch076 [N_Axis]
  Refine = true
  Suppressed = false
  Type = 0
FEATURE [Sketcher::SketchObject] Sketch077
  ArcFitTolerance = 1e-06
  AttachmentSupport = -> [Pad062]
  ExternalGeometry = -> [Pad062]
  FullyConstrained = true
  MakeInternals = false
  MapMode = 5
  Placement = pos=(5.47474,0,5.59e-14) rot=(0.57735,0.57735,0.57735;2.0944rad)
  sketch-geometry (4):
    g0: LineSegment StartX=-13.8 StartY=1 StartZ=0 EndX=-20.8 EndY=1 EndZ=0
    g1: LineSegment StartX=-20.8 StartY=1 StartZ=0 EndX=-20.8 EndY=-11 EndZ=0
    g2: LineSegment StartX=-20.8 StartY=-11 StartZ=0 EndX=-13.8 EndY=-11 EndZ=0
    g3: LineSegment StartX=-13.8 StartY=-11 StartZ=0 EndX=-13.8 EndY=1 EndZ=0
  constraints (10):
    c: Coincident(g0,g1)
    c: Coincident(g1,g2)
    c: Coincident(g2,g3)
    c: Coincident(g3,g0)
    c: Horizontal(g0)
    c: Horizontal(g2)
    c: Vertical(g1)
    c: Coincident(g0,g-3)
    c: DistanceX(g0,g0) = 7
    c: Coincident(g2,g-3)
FEATURE [PartDesign::Pad] Pad063
  BaseFeature = -> Pad062
  Direction = (1,0,1.02e-14)
  Length = 6
  Length2 = 10
  Profile = -> Sketch077
  ReferenceAxis = -> Sketch077 [N_Axis]
  Refine = true
  Reversed = true
  Suppressed = false
  Type = 0
FEATURE [Sketcher::SketchObject] Sketch079
  ArcFitTolerance = 1e-06
  AttachmentSupport = -> [Pad063]
  ExternalGeometry = -> [Pad063]
  FullyConstrained = true
  MakeInternals = false
  MapMode = 5
  Placement = pos=(1.116e-13,0,-11) rot=(1,0,0;3.14159rad)
  sketch-geometry (4):
    g0: LineSegment StartX=5.47474 StartY=20.8 StartZ=0 EndX=-0.525259 EndY=20.8 EndZ=0
    g1: LineSegment StartX=-0.525259 StartY=20.8 StartZ=0 EndX=-0.525259 EndY=13.8 EndZ=0
    g2: LineSegment StartX=-0.525259 StartY=13.8 StartZ=0 EndX=5.47474 EndY=13.8 EndZ=0
    g3: LineSegment StartX=5.47474 StartY=13.8 StartZ=0 EndX=5.47474 EndY=20.8 EndZ=0
  constraints (10):
    c: Coincident(g0,g1)
    c: Coincident(g1,g2)
    c: Coincident(g2,g3)
    c: Coincident(g3,g0)
    c: Horizontal(g0)
    c: Horizontal(g2)
    c: Vertical(g1)
    c: Vertical(g3)
    c: Coincident(g0,g-3)
    c: Coincident(g1,g-5)
FEATURE [PartDesign::Pocket] Pocket185
  BaseFeature = -> Pad063
  Direction = (-1.01e-14,0,1)
  Length = 2.9
  Length2 = 5
  Profile = -> Sketch079
  ReferenceAxis = -> Sketch079 [N_Axis]
  Refine = true
  Suppressed = false
  Type = 0
FEATURE [Sketcher::SketchObject] Sketch080
  ArcFitTolerance = 1e-06
  AttachmentSupport = -> [Pocket185]
  ExternalGeometry = -> [Pocket185]
  FullyConstrained = true
  MakeInternals = false
  MapMode = 5
  Placement = pos=(3.47474,0,3.55e-14) rot=(0.57735,-0.57735,-0.57735;2.0944rad)
  sketch-geometry (4):
    g0: Circle CenterX=6.5 CenterY=-8.1 CenterZ=0 NormalX=0 NormalY=0 NormalZ=1 AngleXU=0 Radius=2.25
    g1: Circle CenterX=-7.5 CenterY=-8.1 CenterZ=0 NormalX=0 NormalY=0 NormalZ=1 AngleXU=0 Radius=2.25
    g2: Circle CenterX=-7.5 CenterY=-8.1 CenterZ=0 NormalX=0 NormalY=0 NormalZ=1 AngleXU=0 Radius=5
    g3: Circle CenterX=6.5 CenterY=-8.1 CenterZ=0 NormalX=0 NormalY=0 NormalZ=1 AngleXU=0 Radius=5
  constraints (10):
    c: Diameter(g0) = 4.5
    c: Diameter(g1) = 4.5
    c: DistanceY(g-4,g0) = 0
    c: DistanceY(g0,g1) = 0
    c: DistanceX(g1,g0) = 14
    c: DistanceX(g-5,g1) = 9
    c: Coincident(g2,g1)
    c: Coincident(g3,g0)
    c: Diameter(g2) = 10
    c: Diameter(g3) = 10
FEATURE [PartDesign::Pad] Pad064
  BaseFeature = -> Pocket185
  Direction = (-1,0,-1.02e-14)
  Length = 2
  Length2 = 10
  Profile = -> Sketch080
  ReferenceAxis = -> Sketch080 [N_Axis]
  Refine = true
  Reversed = true
  Suppressed = false
  Type = 0
FEATURE [Sketcher::SketchObject] Sketch081
  ArcFitTolerance = 1e-06
  AttachmentSupport = -> [Pad064]
  ExternalGeometry = -> [Pad064]
  FullyConstrained = true
  MakeInternals = false
  MapMode = 5
  Placement = pos=(3.47474,0,3.55e-14) rot=(0.57735,-0.57735,-0.57735;2.0944rad)
  sketch-geometry (1):
    g0: Circle CenterX=-1.5 CenterY=-5 CenterZ=0 NormalX=0 NormalY=0 NormalZ=1 AngleXU=0 Radius=2.1
  constraints (2):
    c: Coincident(g0,g-4)
    c: Equal(g0,g-4)
FEATURE [PartDesign::Pocket] Pocket186
  BaseFeature = -> Pad064
  Direction = (1,0,1.02e-14)
  Length = 4.7
  Length2 = 5
  Profile = -> Sketch081
  ReferenceAxis = -> Sketch081 [N_Axis]
  Refine = true
  Suppressed = false
  Type = 0
FEATURE [PartDesign::Pad] Pad065
  BaseFeature = -> Pocket186
  Direction = (-1,0,-1.02e-14)
  Length = 2
  Length2 = 10
  Profile = -> Sketch080 [Edge2,Edge1]
  ReferenceAxis = -> Sketch080 [N_Axis]
  Refine = true
  Suppressed = false
  Type = 0
FEATURE [Sketcher::SketchObject] Sketch082
  ArcFitTolerance = 1e-06
  AttachmentSupport = -> [Pad065]
  ExternalGeometry = -> [Pad065]
  FullyConstrained = true
  MakeInternals = false
  MapMode = 5
  Placement = pos=(1.47474,0,1.51e-14) rot=(0.57735,-0.57735,-0.57735;2.0944rad)
  sketch-geometry (2):
    g0: Circle CenterX=-7.5 CenterY=-8.1 CenterZ=0 NormalX=0 NormalY=0 NormalZ=1 AngleXU=0 Radius=0.75
    g1: Circle CenterX=6.5 CenterY=-8.1 CenterZ=0 NormalX=0 NormalY=0 NormalZ=1 AngleXU=0 Radius=0.75
  constraints (4):
    c: Coincident(g0,g-4)
    c: Coincident(g1,g-3)
    c: Diameter(g0) = 1.5
    c: Diameter(g1) = 1.5
FEATURE [PartDesign::Pocket] Pocket187
  BaseFeature = -> Pad065
  Direction = (1,0,1.02e-14)
  Length = 5
  Length2 = 5
  Profile = -> Sketch082
  ReferenceAxis = -> Sketch082 [N_Axis]
  Refine = true
  Suppressed = false
  Type = 0
FEATURE [Sketcher::SketchObject] Sketch083
  ArcFitTolerance = 1e-06
  AttachmentSupport = -> [Pocket187]
  ExternalGeometry = -> [Pocket187]
  FullyConstrained = true
  MakeInternals = false
  MapMode = 5
  Placement = pos=(8.16e-14,0,-8.1) rot=(1,0,0;3.14159rad)
  sketch-geometry (1):
    g0: Circle CenterX=2.62474 CenterY=17.35 CenterZ=0 NormalX=0 NormalY=0 NormalZ=1 AngleXU=0 Radius=1.45
  constraints (3):
    c: Diameter(g0) = 2.9
    c: DistanceX(g-3,g0) = 3.15
    c: DistanceY(g0,g-3) = 3.45
FEATURE [PartDesign::Pocket] Pocket188
  BaseFeature = -> Pocket187
  Direction = (-1.01e-14,0,1)
  Length = 10
  Length2 = 5
  Profile = -> Sketch083
  ReferenceAxis = -> Sketch083 [N_Axis]
  Refine = true
  Suppressed = false
  Type = 0
FEATURE [Sketcher::SketchObject] Sketch084
  ArcFitTolerance = 1e-06
  AttachmentSupport = -> [Pocket188]
  ExternalGeometry = -> [Pocket188]
  FullyConstrained = true
  MakeInternals = false
  MapMode = 5
  Placement = pos=(8.16e-14,0,-8.1) rot=(1,0,0;3.14159rad)
  sketch-geometry (3):
    g0: LineSegment StartX=5.47474 StartY=16.8 StartZ=0 EndX=4.27474 EndY=16.8 EndZ=0
    g1: LineSegment StartX=4.27474 StartY=16.8 StartZ=0 EndX=5.47474 EndY=13.8 EndZ=0
    g2: LineSegment StartX=5.47474 StartY=13.8 StartZ=0 EndX=5.47474 EndY=16.8 EndZ=0
  constraints (8):
    c: PointOnObject(g0,g-3)
    c: Horizontal(g0)
    c: Coincident(g1,g0)
    c: Coincident(g1,g-4)
    c: Coincident(g2,g1)
    c: Coincident(g2,g0)
    c: DistanceY(g2,g2) = 3
    c: DistanceX(g0,g0) = 1.2
FEATURE [PartDesign::Pocket] Pocket189
  BaseFeature = -> Pocket188
  Direction = (-1.01e-14,0,1)
  Length = 10
  Length2 = 5
  Profile = -> Sketch084
  ReferenceAxis = -> Sketch084 [N_Axis]
  Refine = true
  Suppressed = false
  Type = 0
FEATURE [Sketcher::SketchObject] Sketch085
  ArcFitTolerance = 1e-06
  AttachmentSupport = -> [Pocket189]
  ExternalGeometry = -> [Pocket189]
  FullyConstrained = true
  MakeInternals = false
  MapMode = 5
  Placement = pos=(5.47474,1.149e-13,2.532e-13) rot=(0.57735,0.57735,0.57735;2.0944rad)
  sketch-geometry (4):
    g0: LineSegment StartX=-20.8 StartY=1 StartZ=0 EndX=-20.8 EndY=-8.1 EndZ=0
    g1: LineSegment StartX=-20.8 StartY=-8.1 StartZ=0 EndX=-16.8 EndY=-8.1 EndZ=0
    g2: LineSegment StartX=-16.8 StartY=-8.1 StartZ=0 EndX=-16.8 EndY=1 EndZ=0
    g3: LineSegment StartX=-16.8 StartY=1 StartZ=0 EndX=-20.8 EndY=1 EndZ=0
  constraints (10):
    c: Coincident(g0,g1)
    c: Coincident(g1,g2)
    c: Coincident(g2,g3)
    c: Coincident(g3,g0)
    c: Vertical(g0)
    c: Vertical(g2)
    c: Horizontal(g1)
    c: Horizontal(g3)
    c: Coincident(g0,g-3)
    c: Coincident(g1,g-4)
FEATURE [PartDesign::Pocket] Pocket190
  BaseFeature = -> Pocket189
  Direction = (-1,-2.09e-14,-4.64e-14)
  Length = 0.2
  Length2 = 5
  Profile = -> Sketch085
  ReferenceAxis = -> Sketch085 [N_Axis]
  Refine = true
  Suppressed = false
  Type = 0
FEATURE [Sketcher::SketchObject] Sketch086
  ArcFitTolerance = 1e-06
  AttachmentSupport = -> [Pocket190]
  ExternalGeometry = -> [Pocket190]
  FullyConstrained = true
  MakeInternals = false
  MapMode = 5
  Placement = pos=(8.16e-14,0,-8.1) rot=(1,0,0;3.14159rad)
  sketch-geometry (3):
    g0: LineSegment StartX=5.27474 StartY=20.8 StartZ=0 EndX=3.97474 EndY=20.8 EndZ=0
    g1: LineSegment StartX=3.97474 StartY=20.8 StartZ=0 EndX=5.27474 EndY=18.8 EndZ=0
    g2: LineSegment StartX=5.27474 StartY=20.8 StartZ=0 EndX=5.27474 EndY=18.8 EndZ=0
  constraints (8):
    c: Coincident(g0,g-4)
    c: PointOnObject(g0,g-3)
    c: Coincident(g1,g0)
    c: PointOnObject(g1,g-4)
    c: Coincident(g2,g0)
    c: Coincident(g2,g1)
    c: DistanceX(g0,g0) = 1.3
    c: DistanceY(g2,g2) = 2
FEATURE [PartDesign::Pocket] Pocket191
  BaseFeature = -> Pocket190
  Direction = (-1.01e-14,0,1)
  Length = 10
  Length2 = 5
  Profile = -> Sketch086
  ReferenceAxis = -> Sketch086 [N_Axis]
  Refine = true
  Suppressed = false
  Type = 0
FEATURE [Sketcher::SketchObject] Sketch087
  ArcFitTolerance = 1e-06
  AttachmentSupport = -> [Pocket191]
  ExternalGeometry = -> [Pocket191]
  FullyConstrained = true
  MakeInternals = false
  MapMode = 5
  Placement = pos=(0,-20.8,0) rot=(1,0,0;1.5708rad)
  sketch-geometry (12):
    g0: LineSegment StartX=-0.525259 StartY=-0.2 StartZ=0 EndX=-0.525259 EndY=-0.4 EndZ=0
    g1: LineSegment StartX=-0.525259 StartY=-0.4 StartZ=0 EndX=3.97474 EndY=-0.4 EndZ=0
    g2: LineSegment StartX=3.97474 StartY=-0.4 StartZ=0 EndX=3.97474 EndY=-0.2 EndZ=0
    g3: LineSegment StartX=3.97474 StartY=-0.2 StartZ=0 EndX=-0.525259 EndY=-0.2 EndZ=0
    g4: LineSegment StartX=-0.525259 StartY=-3.45 StartZ=0 EndX=-0.525259 EndY=-3.65 EndZ=0
    g5: LineSegment StartX=-0.525259 StartY=-3.65 StartZ=0 EndX=3.97474 EndY=-3.65 EndZ=0
    g6: LineSegment StartX=3.97474 StartY=-3.65 StartZ=0 EndX=3.97474 EndY=-3.45 EndZ=0
    g7: LineSegment StartX=3.97474 StartY=-3.45 StartZ=0 EndX=-0.525259 EndY=-3.45 EndZ=0
    g8: LineSegment StartX=-0.525259 StartY=-6.7 StartZ=0 EndX=-0.525259 EndY=-6.9 EndZ=0
    g9: LineSegment StartX=-0.525259 StartY=-6.9 StartZ=0 EndX=3.97474 EndY=-6.9 EndZ=0
    g10: LineSegment StartX=3.97474 StartY=-6.9 StartZ=0 EndX=3.97474 EndY=-6.7 EndZ=0
    g11: LineSegment StartX=3.97474 StartY=-6.7 StartZ=0 EndX=-0.525259 EndY=-6.7 EndZ=0
  constraints (36):
    c: Coincident(g0,g1)
    c: Coincident(g1,g2)
    c: Coincident(g2,g3)
    c: Coincident(g3,g0)
    c: Vertical(g0)
    c: Vertical(g2)
    c: Horizontal(g1)
    c: Horizontal(g3)
    c: PointOnObject(g0,g-3)
    c: PointOnObject(g1,g-4)
    c: Coincident(g4,g5)
    c: Coincident(g5,g6)
    c: Coincident(g6,g7)
    c: Coincident(g7,g4)
    c: Vertical(g4)
    c: Vertical(g6)
    c: Horizontal(g5)
    c: Horizontal(g7)
    c: PointOnObject(g5,g-4)
    c: Coincident(g8,g9)
    c: Coincident(g9,g10)
    c: Coincident(g10,g11)
    c: Coincident(g11,g8)
    c: Vertical(g8)
    c: Vertical(g10)
    c: Horizontal(g9)
    c: Horizontal(g11)
    c: PointOnObject(g8,g-3)
    c: PointOnObject(g9,g-4)
    c: DistanceY(g4,g4) = 0.2
    c: DistanceY(g0,g0) = 0.2
    c: DistanceY(g8,g8) = 0.2
    c: DistanceY(g0,g-3) = 1.2
    c: DistanceY(g-3,g8) = 1.2
    c: DistanceY(g4,g0) = 3.05
    c: PointOnObject(g4,g-3)
FEATURE [PartDesign::Pocket] Pocket192
  BaseFeature = -> Pocket191
  Direction = (0,1,-2e-16)
  Length = 0.2
  Length2 = 5
  Profile = -> Sketch087
  ReferenceAxis = -> Sketch087 [N_Axis]
  Refine = true
  Suppressed = false
  Type = 0
FEATURE [Sketcher::SketchObject] Sketch088
  ArcFitTolerance = 1e-06
  AttachmentSupport = -> [Pocket192]
  ExternalGeometry = -> [Pocket192]
  FullyConstrained = true
  MakeInternals = false
  MapMode = 5
  Placement = pos=(12.2986,-7.99408,1.238e-13) rot=(0.793297,0.430511,0.430511;1.80031rad)
  sketch-geometry (4):
    g0: LineSegment StartX=-15.2734 StartY=-3.45 StartZ=0 EndX=-15.2734 EndY=-3.65 EndZ=0
    g1: LineSegment StartX=-15.2734 StartY=-3.65 StartZ=0 EndX=-12.8881 EndY=-3.65 EndZ=0
    g2: LineSegment StartX=-12.8881 StartY=-3.65 StartZ=0 EndX=-12.8881 EndY=-3.45 EndZ=0
    g3: LineSegment StartX=-12.8881 StartY=-3.45 StartZ=0 EndX=-15.2734 EndY=-3.45 EndZ=0
  constraints (10):
    c: Coincident(g0,g1)
    c: Coincident(g1,g2)
    c: Coincident(g2,g3)
    c: Coincident(g3,g0)
    c: Vertical(g2)
    c: Horizontal(g1)
    c: Horizontal(g3)
    c: Coincident(g0,g-3)
    c: PointOnObject(g1,g-5)
    c: Coincident(g0,g-4)
FEATURE [PartDesign::Pocket] Pocket193
  BaseFeature = -> Pocket192
  Direction = (-0.838444,0.544988,-8.3e-15)
  Length = 0.2
  Length2 = 5
  Profile = -> Sketch088
  ReferenceAxis = -> Sketch088 [N_Axis]
  Refine = true
  Suppressed = false
  Type = 0
FEATURE [Sketcher::SketchObject] Sketch089
  ArcFitTolerance = 1e-06
  AttachmentSupport = -> [Pocket193]
  ExternalGeometry = -> [Pocket193]
  FullyConstrained = true
  MakeInternals = false
  MapMode = 5
  Placement = pos=(5.27474,1.125e-13,2.445e-13) rot=(0.57735,0.57735,0.57735;2.0944rad)
  sketch-geometry (4):
    g0: LineSegment StartX=-18.8 StartY=-3.45 StartZ=0 EndX=-18.8 EndY=-3.65 EndZ=0
    g1: LineSegment StartX=-18.8 StartY=-3.65 StartZ=0 EndX=-16.8 EndY=-3.65 EndZ=0
    g2: LineSegment StartX=-16.8 StartY=-3.65 StartZ=0 EndX=-16.8 EndY=-3.45 EndZ=0
    g3: LineSegment StartX=-16.8 StartY=-3.45 StartZ=0 EndX=-18.8 EndY=-3.45 EndZ=0
  constraints (10):
    c: Coincident(g0,g1)
    c: Coincident(g1,g2)
    c: Coincident(g2,g3)
    c: Coincident(g3,g0)
    c: Vertical(g2)
    c: Horizontal(g1)
    c: Horizontal(g3)
    c: Coincident(g0,g-3)
    c: PointOnObject(g1,g-5)
    c: Coincident(g0,g-4)
FEATURE [PartDesign::Pocket] Pocket194
  BaseFeature = -> Pocket193
  Direction = (-1,-2.14e-14,-4.63e-14)
  Length = 0.2
  Length2 = 5
  Profile = -> Sketch089
  ReferenceAxis = -> Sketch089 [N_Axis]
  Refine = true
  Suppressed = false
  Type = 0
FEATURE [Sketcher::SketchObject] Sketch090
  ArcFitTolerance = 1e-06
  AttachmentSupport = -> [Pocket194]
  ExternalGeometry = -> [Pocket194]
  FullyConstrained = true
  MakeInternals = false
  MapMode = 5
  Placement = pos=(0,-16.8,0) rot=(0,0.707107,0.707107;3.14159rad)
  sketch-geometry (4):
    g0: LineSegment StartX=-5.27474 StartY=-3.45 StartZ=0 EndX=-5.27474 EndY=-3.65 EndZ=0
    g1: LineSegment StartX=-5.27474 StartY=-3.65 StartZ=0 EndX=-4.27474 EndY=-3.65 EndZ=0
    g2: LineSegment StartX=-4.27474 StartY=-3.65 StartZ=0 EndX=-4.27474 EndY=-3.45 EndZ=0
    g3: LineSegment StartX=-4.27474 StartY=-3.45 StartZ=0 EndX=-5.27474 EndY=-3.45 EndZ=0
  constraints (11):
    c: Coincident(g0,g1)
    c: Coincident(g1,g2)
    c: Coincident(g2,g3)
    c: Coincident(g3,g0)
    c: Vertical(g0)
    c: Vertical(g2)
    c: Horizontal(g1)
    c: Horizontal(g3)
    c: Coincident(g0,g-4)
    c: PointOnObject(g1,g-3)
    c: PointOnObject(g-5,g1)
FEATURE [PartDesign::Pocket] Pocket195
  BaseFeature = -> Pocket194
  Direction = (0,-1,2e-16)
  Length = 0.2
  Length2 = 5
  Profile = -> Sketch090
  ReferenceAxis = -> Sketch090 [N_Axis]
  Refine = true
  Suppressed = false
  Type = 0
FEATURE [Sketcher::SketchObject] Sketch091
  ArcFitTolerance = 1e-06
  AttachmentSupport = -> [Pocket195]
  ExternalGeometry = -> [Pocket195]
  FullyConstrained = true
  MakeInternals = false
  MapMode = 5
  Placement = pos=(8.16e-14,0,-8.1) rot=(1,0,0;3.14159rad)
  sketch-geometry (6):
    g0: LineSegment StartX=3.97474 StartY=20.8 StartZ=0 EndX=5.27474 EndY=18.8 EndZ=0
    g1: LineSegment StartX=5.27474 StartY=18.8 StartZ=0 EndX=5.27474 EndY=16.8 EndZ=0
    g2: LineSegment StartX=5.27474 StartY=16.8 StartZ=0 EndX=4.77474 EndY=16.8 EndZ=0
    g3: LineSegment StartX=4.77474 StartY=16.8 StartZ=0 EndX=4.77474 EndY=18.8 EndZ=0
    g4: LineSegment StartX=4.77474 StartY=18.8 StartZ=0 EndX=3.47474 EndY=20.8 EndZ=0
    g5: LineSegment StartX=3.47474 StartY=20.8 StartZ=0 EndX=3.97474 EndY=20.8 EndZ=0
  constraints (15):
    c: Coincident(g0,g-4)
    c: Coincident(g0,g-5)
    c: Coincident(g1,g0)
    c: Coincident(g1,g-6)
    c: Coincident(g2,g1)
    c: Coincident(g3,g2)
    c: Vertical(g3)
    c: Coincident(g4,g3)
    c: PointOnObject(g4,g-4)
    c: Coincident(g5,g4)
    c: Coincident(g5,g0)
    c: Parallel(g4,g0)
    c: DistanceX(g5,g5) = 0.5
    c: DistanceX(g2,g2) = 0.5
    c: PointOnObject(g2,g-6)
FEATURE [PartDesign::Body] Body006  label="Right_Arm"
  AllowCompound = false
  Group = -> [Binder002,Sketch071,Pad058,Sketch072,Pad059,Sketch073,Pocket183,Pad060,Sketch074,Pocket184,Sketch075,Pad061,Sketch076,Pad062,Sketch077,Pad063,Sketch079,Pocket185,Sketch080,Pad064,Sketch081,Pocket186,Pad065,Sketch082,Pocket187,Sketch083,Pocket188,Sketch084,Pocket189,Sketch085,Pocket190,Sketch086,Pocket191,Sketch087,Pocket192,Sketch088,Pocket193,Sketch089,Pocket194,Sketch090,Pocket195,Sketch091,+15 more]
  Origin = -> Origin007
  Placement = pos=(27.53,19,0) rot=(0,0,1;0rad)
  Tip = -> Pocket219
COMPONENT P20 — same part as P18; its construction recipe is shown at P18.
COMPONENT P21 — same part as P18; its construction recipe is shown at P18.
COMPONENT P22 — same part as P18; its construction recipe is shown at P18.
COMPONENT P23 — same part as P18; its construction recipe is shown at P18.
COMPONENT P24 — geometry summary ("Head"; no construction recipe available for this part):
  bounding box: 9.2 x 8.2 x 7.1 mm
  tessellated surface: 4,146 triangles
  volume: 316 mm^3 (58% of its bounding box)
  symmetry: mirror-symmetric across its x mid-plane
PROVENANCE & LICENSES
A FreeCAD (.FCStd) document from a public repository crawl; recipes are the document's own serialized feature recipes (and, for linked parts, companion documents' recipes).
License: as declared in the source repository (recorded in the dataset sidecar).
